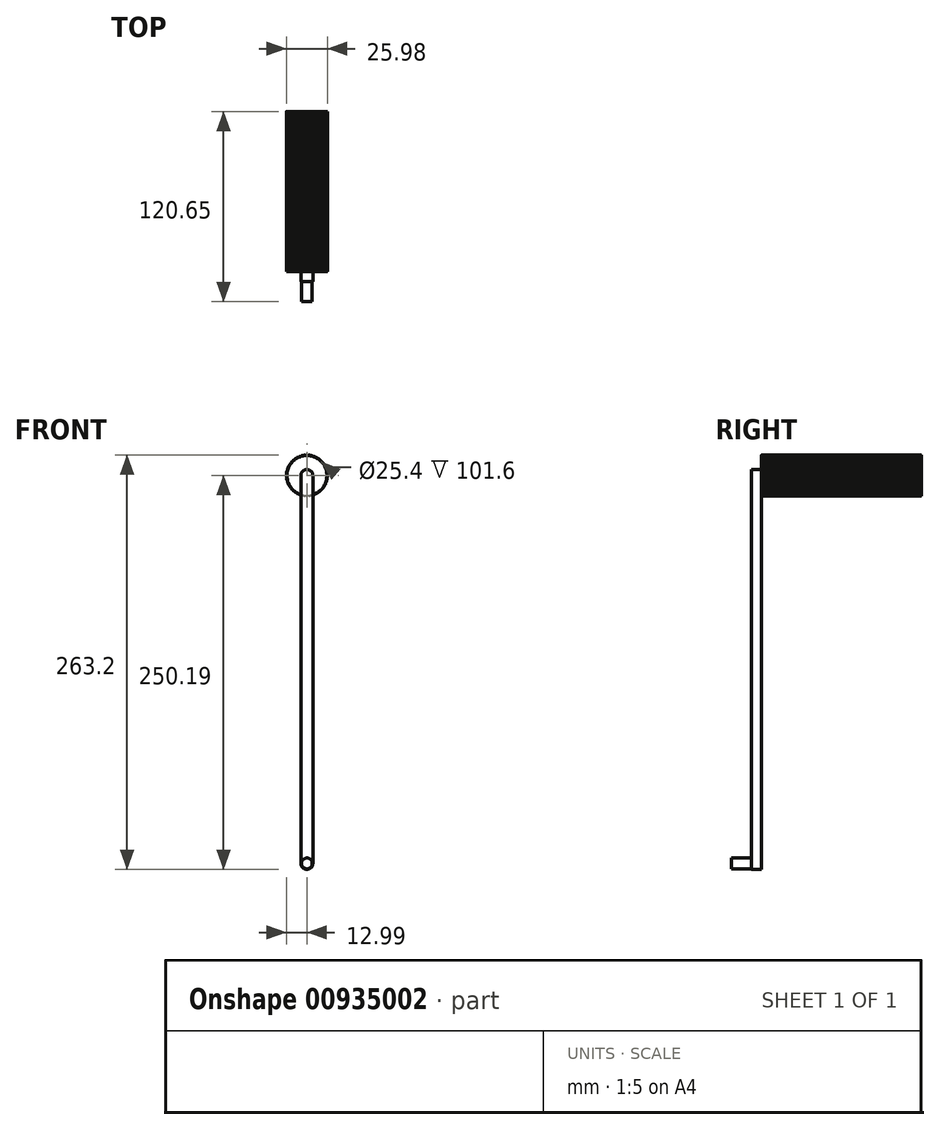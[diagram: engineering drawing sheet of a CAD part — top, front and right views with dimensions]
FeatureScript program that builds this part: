
annotation { "Feature Type Name" : "Feature", "Feature Type Description" : "" }
export const myFeature = defineFeature(function(context is Context, id is Id, definition is map)
    precondition{}
    {
        {
            var Q0;
            Q0=qCreatedBy(makeId("Front.planeOp"),FACE);
            var sketch = newSketch(context, id + "F0", { "sketchPlane" : qUnion([Q0])});
            skLineSegment(sketch, "E0.bottom", {"start": v(0, 127) * mm, "end": v(0, 127) * mm});
            skLineSegment(sketch, "E0.top", {"start": v(0, -127) * mm, "end": v(0, -127) * mm});
            skLineSegment(sketch, "E0.left", {"start": v(3.8, 123.19) * mm, "end": v(3.81, -123.2) * mm});
            skLineSegment(sketch, "E0.right", {"start": v(-3.81, 123.19) * mm, "end": v(-3.8, -123.2) * mm});
            skPoint(sketch, "E0.middle", {"position": v(0, 0) * mm});
            skPoint(sketch, "E1.visualSharp", {"position": v(-3.81, 127) * mm});
            skArc(sketch, "E1.filletArc", {"start": v(0, 127) * mm, "mid": v(-2.7, 125.88) * mm, "end": v(-3.81, 123.19) * mm});
            skPoint(sketch, "E2.visualSharp", {"position": v(3.8, 127) * mm});
            skArc(sketch, "E2.filletArc", {"start": v(3.8, 123.19) * mm, "mid": v(2.7, 125.88) * mm, "end": v(0, 127) * mm});
            skPoint(sketch, "E3.visualSharp", {"position": v(-3.8, -127) * mm});
            skArc(sketch, "E3.filletArc", {"start": v(-3.8, -123.2) * mm, "mid": v(-2.7, -125.88) * mm, "end": v(0, -127) * mm});
            skPoint(sketch, "E4.visualSharp", {"position": v(3.81, -127) * mm});
            skArc(sketch, "E4.filletArc", {"start": v(0, -127) * mm, "mid": v(2.7, -125.88) * mm, "end": v(3.81, -123.2) * mm});
            skSolve(sketch);
        }
        {
            var Q0;
            Q0 = qSketchRegion(id + "F0", true);
            extrude(context, id + "F1", {"entities" : qUnion([Q0]), "depth" : 6.35 * mm, "offsetDistance" : 25.4 * mm});
        }
        {
            var Q0;
            Q0=makeQuery(id+"F1.opExtrude","CAP_FACE",FACE,{"disambiguationData":[OSD([sQuery(id+"F0.wireOp",EDGE,"E0.left"),sQuery(id+"F0.wireOp",EDGE,"E0.right"),sQuery(id+"F0.wireOp",EDGE,"E1.filletArc"),sQuery(id+"F0.wireOp",EDGE,"E2.filletArc"),sQuery(id+"F0.wireOp",EDGE,"E3.filletArc"),sQuery(id+"F0.wireOp",EDGE,"E4.filletArc")])],"isStart":false});
            var sketch = newSketch(context, id + "F2", { "sketchPlane" : qUnion([Q0])});
            skCircle(sketch, "E5", {"center": v(0, -123.2) * mm, "radius": 3.4 * mm});
            skSolve(sketch);
        }
        {
            var Q0;
            Q0 = qSketchRegion(id + "F2", true);
            extrude(context, id + "F3", {"entities" : qUnion([Q0]), "operationType" : NewBodyOperationType.ADD, "depth" : 12.7 * mm, "offsetDistance" : 25.4 * mm});
        }
        {
            var Q0;
            Q0=makeQuery(id+"F1.opExtrude","CAP_FACE",FACE,{"disambiguationData":[OSD([sQuery(id+"F0.wireOp",EDGE,"E0.left"),sQuery(id+"F0.wireOp",EDGE,"E0.right"),sQuery(id+"F0.wireOp",EDGE,"E1.filletArc"),sQuery(id+"F0.wireOp",EDGE,"E2.filletArc"),sQuery(id+"F0.wireOp",EDGE,"E3.filletArc"),sQuery(id+"F0.wireOp",EDGE,"E4.filletArc")])],"isStart":true});
            var sketch = newSketch(context, id + "F4", { "sketchPlane" : qUnion([Q0])});
            skCircle(sketch, "E6", {"center": v(0, 123.19) * mm, "radius": 12.7 * mm});
            skCircle(sketch, "E7", {"center": v(0, 134.93) * mm, "radius": 1.27 * mm});
            skCircle(sketch, "E8.1.0", {"center": v(-1.47, 134.84) * mm, "radius": 1.27 * mm});
            skCircle(sketch, "E8.2.0", {"center": v(-2.92, 134.56) * mm, "radius": 1.27 * mm});
            skCircle(sketch, "E8.3.0", {"center": v(-4.32, 134.1) * mm, "radius": 1.27 * mm});
            skCircle(sketch, "E8.4.0", {"center": v(-5.66, 133.48) * mm, "radius": 1.27 * mm});
            skCircle(sketch, "E8.5.0", {"center": v(-6.9, 132.69) * mm, "radius": 1.27 * mm});
            skCircle(sketch, "E8.6.0", {"center": v(-8.04, 131.75) * mm, "radius": 1.27 * mm});
            skCircle(sketch, "E8.7.0", {"center": v(-9.05, 130.67) * mm, "radius": 1.27 * mm});
            skCircle(sketch, "E8.8.0", {"center": v(-9.91, 129.48) * mm, "radius": 1.27 * mm});
            skCircle(sketch, "E8.9.0", {"center": v(-10.62, 128.19) * mm, "radius": 1.27 * mm});
            skCircle(sketch, "E8.10.0", {"center": v(-11.17, 126.82) * mm, "radius": 1.27 * mm});
            skCircle(sketch, "E8.11.0", {"center": v(-11.53, 125.4) * mm, "radius": 1.27 * mm});
            skCircle(sketch, "E8.12.0", {"center": v(-11.72, 123.93) * mm, "radius": 1.27 * mm});
            skCircle(sketch, "E8.13.0", {"center": v(-11.72, 122.45) * mm, "radius": 1.27 * mm});
            skCircle(sketch, "E8.14.0", {"center": v(-11.53, 120.99) * mm, "radius": 1.27 * mm});
            skCircle(sketch, "E8.15.0", {"center": v(-11.17, 119.56) * mm, "radius": 1.27 * mm});
            skCircle(sketch, "E8.16.0", {"center": v(-10.62, 118.2) * mm, "radius": 1.27 * mm});
            skCircle(sketch, "E8.17.0", {"center": v(-9.91, 116.9) * mm, "radius": 1.27 * mm});
            skCircle(sketch, "E8.18.0", {"center": v(-9.05, 115.7) * mm, "radius": 1.27 * mm});
            skCircle(sketch, "E8.19.0", {"center": v(-8.04, 114.63) * mm, "radius": 1.27 * mm});
            skCircle(sketch, "E8.20.0", {"center": v(-6.9, 113.7) * mm, "radius": 1.27 * mm});
            skCircle(sketch, "E8.21.0", {"center": v(-5.66, 112.9) * mm, "radius": 1.27 * mm});
            skCircle(sketch, "E8.22.0", {"center": v(-4.32, 112.27) * mm, "radius": 1.27 * mm});
            skCircle(sketch, "E8.23.0", {"center": v(-2.92, 111.82) * mm, "radius": 1.27 * mm});
            skCircle(sketch, "E8.24.0", {"center": v(-1.47, 111.54) * mm, "radius": 1.27 * mm});
            skCircle(sketch, "E8.25.0", {"center": v(0, 111.45) * mm, "radius": 1.27 * mm});
            skCircle(sketch, "E8.26.0", {"center": v(1.47, 111.54) * mm, "radius": 1.27 * mm});
            skCircle(sketch, "E8.27.0", {"center": v(2.92, 111.82) * mm, "radius": 1.27 * mm});
            skCircle(sketch, "E8.28.0", {"center": v(4.32, 112.27) * mm, "radius": 1.27 * mm});
            skCircle(sketch, "E8.29.0", {"center": v(5.66, 112.9) * mm, "radius": 1.27 * mm});
            skCircle(sketch, "E8.30.0", {"center": v(6.9, 113.7) * mm, "radius": 1.27 * mm});
            skCircle(sketch, "E8.31.0", {"center": v(8.04, 114.63) * mm, "radius": 1.27 * mm});
            skCircle(sketch, "E8.32.0", {"center": v(9.05, 115.7) * mm, "radius": 1.27 * mm});
            skCircle(sketch, "E8.33.0", {"center": v(9.91, 116.9) * mm, "radius": 1.27 * mm});
            skCircle(sketch, "E8.34.0", {"center": v(10.62, 118.2) * mm, "radius": 1.27 * mm});
            skCircle(sketch, "E8.35.0", {"center": v(11.17, 119.56) * mm, "radius": 1.27 * mm});
            skCircle(sketch, "E8.36.0", {"center": v(11.53, 120.99) * mm, "radius": 1.27 * mm});
            skCircle(sketch, "E8.37.0", {"center": v(11.72, 122.45) * mm, "radius": 1.27 * mm});
            skCircle(sketch, "E8.38.0", {"center": v(11.72, 123.93) * mm, "radius": 1.27 * mm});
            skCircle(sketch, "E8.39.0", {"center": v(11.53, 125.4) * mm, "radius": 1.27 * mm});
            skCircle(sketch, "E8.40.0", {"center": v(11.17, 126.82) * mm, "radius": 1.27 * mm});
            skCircle(sketch, "E8.41.0", {"center": v(10.62, 128.19) * mm, "radius": 1.27 * mm});
            skCircle(sketch, "E8.42.0", {"center": v(9.91, 129.48) * mm, "radius": 1.27 * mm});
            skCircle(sketch, "E8.43.0", {"center": v(9.05, 130.67) * mm, "radius": 1.27 * mm});
            skCircle(sketch, "E8.44.0", {"center": v(8.04, 131.75) * mm, "radius": 1.27 * mm});
            skCircle(sketch, "E8.45.0", {"center": v(6.9, 132.69) * mm, "radius": 1.27 * mm});
            skCircle(sketch, "E8.46.0", {"center": v(5.66, 133.48) * mm, "radius": 1.27 * mm});
            skCircle(sketch, "E8.47.0", {"center": v(4.32, 134.1) * mm, "radius": 1.27 * mm});
            skCircle(sketch, "E8.48.0", {"center": v(2.92, 134.56) * mm, "radius": 1.27 * mm});
            skCircle(sketch, "E8.49.0", {"center": v(1.47, 134.84) * mm, "radius": 1.27 * mm});
            skSolve(sketch);
        }
        {
            var Q0;
            Q0 = qSketchRegion(id + "F4", true);
            extrude(context, id + "F5", {"entities" : qUnion([Q0]), "operationType" : NewBodyOperationType.ADD, "depth" : 101.6 * mm, "offsetDistance" : 25.4 * mm});
        }
    });
